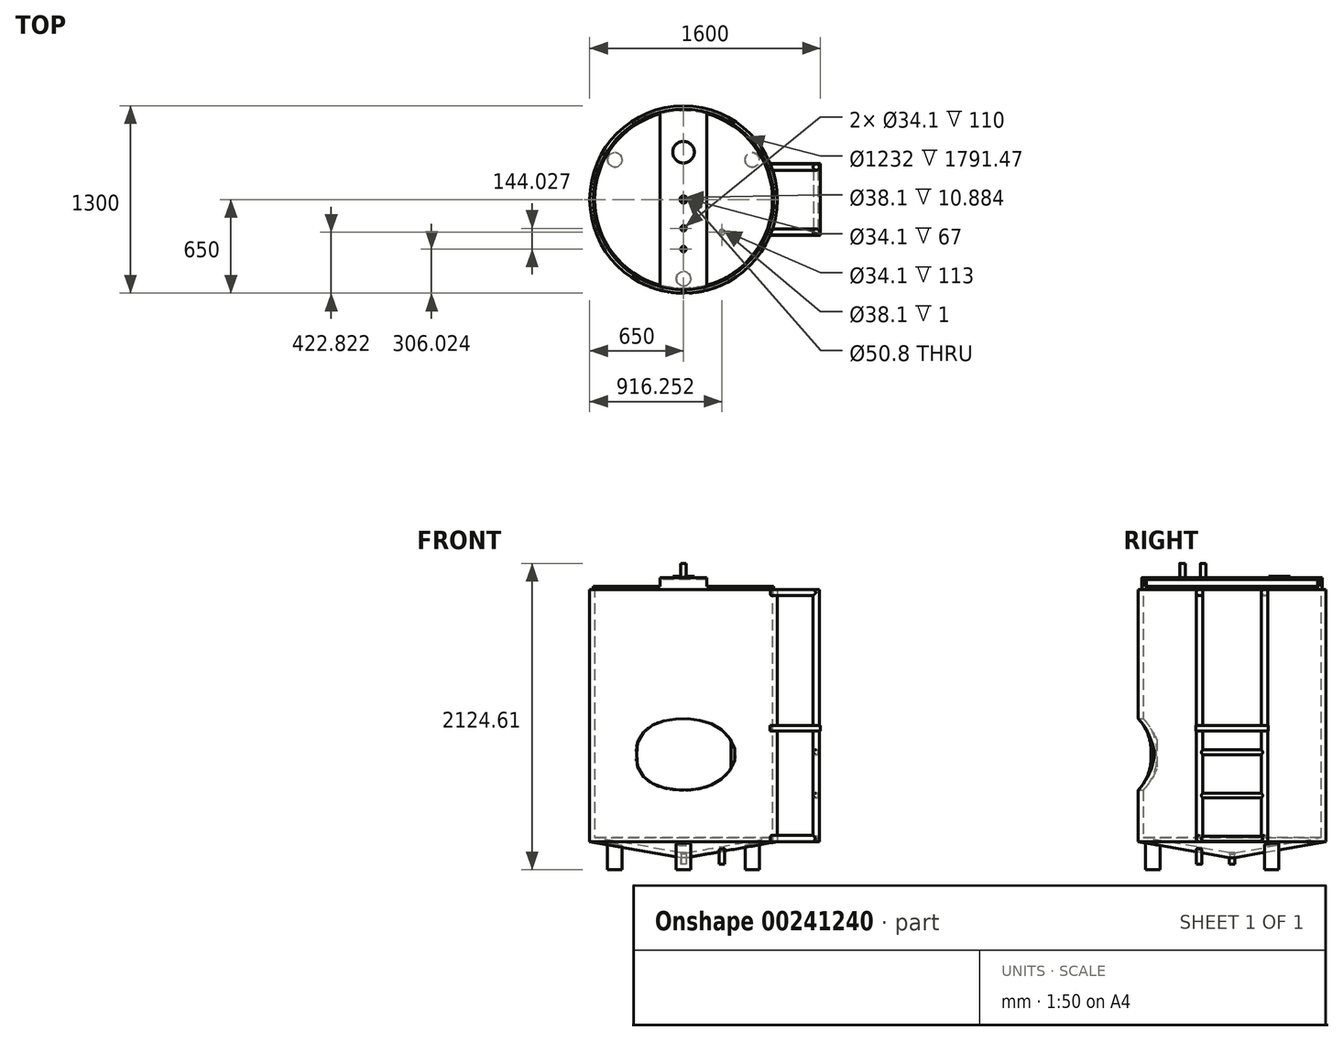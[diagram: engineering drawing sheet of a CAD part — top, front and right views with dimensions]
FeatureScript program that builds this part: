
annotation { "Feature Type Name" : "Feature", "Feature Type Description" : "" }
export const myFeature = defineFeature(function(context is Context, id is Id, definition is map)
    precondition{}
    {
        {
            var Q0;
            Q0=qCreatedBy(makeId("Front.planeOp"),FACE);
            var sketch = newSketch(context, id + "F0", { "sketchPlane" : qUnion([Q0])});
            skLineSegment(sketch, "E0", {"start": v(0, 0) * mm, "end": v(650, 114.61) * mm});
            skLineSegment(sketch, "E1", {"start": v(650, 114.61) * mm, "end": v(650, 1864.61) * mm});
            skLineSegment(sketch, "E2", {"start": v(650, 1864.61) * mm, "end": v(0, 1864.61) * mm});
            skLineSegment(sketch, "E3", {"start": v(0, 0) * mm, "end": v(0, 1864.61) * mm});
            skSolve(sketch);
        }
        {
            var Q0;
            Q0 = qSketchRegion(id + "F0", true);
            var Q1;
            Q1=sQuery(id+"F0.wireOp",EDGE,"E3");
            revolve(context, id + "F1", {"entities" : qUnion([Q0]), "axis" : qUnion([Q1]), "revolveType" : RevolveType.FULL});
        }
        {
            var Q0;
            Q0=makeQuery(id+"F1.opRevolve","SWEPT_FACE",FACE,{"disambiguationData":[OSD([sQuery(id+"F0.wireOp",EDGE,"E2")])]});
            shell(context, id + "F2", {"entities" : qUnion([Q0]), "thickness" : 34 * mm});
        }
        {
            var Q0;
            Q0=qCreatedBy(makeId("Top.planeOp"),FACE);
            cPlane(context, id + "F3", {"entities" : qUnion([Q0]), "cplaneType" : CPlaneType.OFFSET, "offset" : 280 * mm, "oppositeDirection" : true, "width" : 150 * mm, "height" : 150 * mm});
        }
        {
            var Q0;
            Q0=qCreatedBy(id+"F3.planeOp",FACE);
            var sketch = newSketch(context, id + "F4", { "sketchPlane" : qUnion([Q0])});
            skCircle(sketch, "E4", {"center": v(0, -550) * mm, "radius": 50 * mm});
            skCircle(sketch, "E5", {"center": v(476.31, 275) * mm, "radius": 50 * mm});
            skCircle(sketch, "E6", {"center": v(-476.31, 275) * mm, "radius": 50 * mm});
            skSolve(sketch);
        }
        {
            var Q0;
            Q0 = qSketchRegion(id + "F4", true);
            var Q1;
            Q1=makeQuery(id+"F1.opRevolve","SWEPT_BODY",BODY,{"disambiguationData":[OSD([sQuery(id+"F0.wireOp",EDGE,"E0"),sQuery(id+"F0.wireOp",EDGE,"E1"),sQuery(id+"F0.wireOp",EDGE,"E2"),sQuery(id+"F0.wireOp",EDGE,"E3")])]});
            extrude(context, id + "F5", {"entities" : qUnion([Q0]), "operationType" : NewBodyOperationType.ADD, "endBound" : BoundingType.UP_TO_BODY, "endBoundEntityBody" : qUnion([Q1]), "depth" : 25 * mm});
        }
        {
            var Q0;
            Q0=makeQuery(id+"F5.opExtrude","CAP_FACE",FACE,{"disambiguationData":[OSD([sQuery(id+"F4.wireOp",EDGE,"E5")])],"isStart":true});
            var sketch = newSketch(context, id + "F6", { "sketchPlane" : qUnion([Q0])});
            skCircle(sketch, "E7.0", {"center": v(476.31, -275) * mm, "radius": 50 * mm});
            skCircle(sketch, "E8.0", {"center": v(0, 550) * mm, "radius": 50 * mm});
            skCircle(sketch, "E9.0", {"center": v(-476.31, -275) * mm, "radius": 50 * mm});
            skSolve(sketch);
        }
        {
            var Q0;
            Q0 = qSketchRegion(id + "F6", true);
            extrude(context, id + "F7", {"entities" : qUnion([Q0]), "operationType" : NewBodyOperationType.REMOVE, "oppositeDirection" : true, "depth" : 200 * mm});
        }
        {
            var Q0;
            Q0=qCreatedBy(makeId("Top.planeOp"),FACE);
            var sketch = newSketch(context, id + "F8", { "sketchPlane" : qUnion([Q0])});
            skCircle(sketch, "E10", {"center": v(0, 0) * mm, "radius": 19.05 * mm});
            skCircle(sketch, "E11", {"center": v(266.25, -227.18) * mm, "radius": 19.05 * mm});
            skSolve(sketch);
        }
        {
            var Q0;
            Q0 = qSketchRegion(id + "F8", true);
            extrude(context, id + "F9", {"entities" : qUnion([Q0]), "operationType" : NewBodyOperationType.REMOVE, "depth" : 74 * mm});
        }
        {
            var Q0;
            Q0=makeQuery(id+"F1.opRevolve","SWEPT_FACE",FACE,{"disambiguationData":[OSD([sQuery(id+"F0.wireOp",EDGE,"E2")])]});
            var sketch = newSketch(context, id + "F10", { "sketchPlane" : qUnion([Q0])});
            skCircle(sketch, "E12.0", {"center": v(0, 0) * mm, "radius": 616 * mm});
            skCircle(sketch, "E13.0", {"center": v(0, 0) * mm, "radius": 626 * mm});
            skSolve(sketch);
        }
        {
            var Q0;
            Q0 = qSketchRegion(id + "F10", true);
            extrude(context, id + "F11", {"entities" : qUnion([Q0]), "operationType" : NewBodyOperationType.ADD, "depth" : 20 * mm});
        }
        {
            var Q0;
            Q0=qCreatedBy(makeId("Front.planeOp"),FACE);
            cPlane(context, id + "F12", {"entities" : qUnion([Q0]), "cplaneType" : CPlaneType.OFFSET, "offset" : 670 * mm, "width" : 150 * mm, "height" : 150 * mm});
        }
        {
            var Q0;
            Q0=qCreatedBy(id+"F12.planeOp",FACE);
            var sketch = newSketch(context, id + "F13", { "sketchPlane" : qUnion([Q0])});
            skLineSegment(sketch, "E14", {"start": v(0, 720) * mm, "end": v(325, 720) * mm});
            skLineSegment(sketch, "E15", {"start": v(0, 720) * mm, "end": v(-325, 720) * mm});
            skLineSegment(sketch, "E16", {"start": v(0, 720) * mm, "end": v(0, 945) * mm});
            skLineSegment(sketch, "E17", {"start": v(0, 720) * mm, "end": v(0, 495) * mm});
            skLineSegment(sketch, "E18", {"start": v(234.5, 720) * mm, "end": v(234.5, 875.8) * mm});
            skLineSegment(sketch, "E19", {"start": v(234.5, 720) * mm, "end": v(234.5, 564.2) * mm});
            skLineSegment(sketch, "E20", {"start": v(-234.5, 720) * mm, "end": v(-234.5, 875.8) * mm});
            skLineSegment(sketch, "E21", {"start": v(-234.5, 720) * mm, "end": v(-234.5, 564.2) * mm});
            skFitSpline(sketch, "E22", {"points": [v(-325, 720) * mm, v(-234.5, 875.8) * mm, v(0, 945) * mm, v(234.5, 875.8) * mm, v(325, 720) * mm, v(234.5, 564.2) * mm, v(0, 495) * mm, v(-234.5, 564.2) * mm, v(-325, 720) * mm]});
            skFitSpline(sketch, "E23.0", {"points": [v(-334.9, 713.7) * mm, v(-335.05, 720) * mm, v(-334.9, 726.3) * mm, v(-334.38, 734.68) * mm, v(-333.06, 745.1) * mm, v(-330.5, 757.5) * mm, v(-325.81, 773.84) * mm, v(-317.72, 793.8) * mm, v(-304.75, 816.76) * mm, v(-288.86, 838.5) * mm, v(-273.43, 855.42) * mm, v(-259.92, 868.1) * mm, v(-249.25, 877.16) * mm, v(-238.06, 885.74) * mm, v(-226.41, 893.8) * mm, v(-214.33, 901.33) * mm, v(-197.68, 910.7) * mm, v(-175.93, 921.14) * mm, v(-148.54, 931.68) * mm, v(-110.62, 943.1) * mm, v(-71, 950.64) * mm, v(-30.55, 954.38) * mm, v(0, 955.31) * mm, v(30.55, 954.38) * mm, v(71, 950.64) * mm, v(110.62, 943.1) * mm, v(148.54, 931.68) * mm, v(175.93, 921.14) * mm, v(197.68, 910.7) * mm, v(214.33, 901.33) * mm, v(226.41, 893.8) * mm, v(238.06, 885.74) * mm, v(249.25, 877.16) * mm, v(259.92, 868.1) * mm, v(273.43, 855.42) * mm, v(288.86, 838.5) * mm, v(304.75, 816.76) * mm, v(317.72, 793.8) * mm, v(325.81, 773.84) * mm, v(330.5, 757.5) * mm, v(333.06, 745.1) * mm, v(334.38, 734.68) * mm, v(334.9, 726.3) * mm, v(335.05, 720) * mm, v(334.9, 713.7) * mm, v(334.38, 705.32) * mm, v(333.06, 694.9) * mm, v(330.5, 682.5) * mm, v(325.81, 666.16) * mm, v(317.72, 646.2) * mm, v(304.75, 623.24) * mm, v(288.86, 601.5) * mm, v(273.43, 584.58) * mm, v(259.92, 571.9) * mm, v(249.25, 562.84) * mm, v(238.06, 554.26) * mm, v(226.41, 546.2) * mm, v(214.33, 538.67) * mm, v(197.68, 529.3) * mm, v(175.93, 518.86) * mm, v(148.54, 508.32) * mm, v(110.62, 496.9) * mm, v(71, 489.36) * mm, v(30.55, 485.62) * mm, v(0, 484.69) * mm, v(-30.55, 485.62) * mm, v(-71, 489.36) * mm, v(-110.62, 496.9) * mm, v(-148.54, 508.32) * mm, v(-175.93, 518.86) * mm, v(-197.68, 529.3) * mm, v(-214.33, 538.67) * mm, v(-226.41, 546.2) * mm, v(-238.06, 554.26) * mm, v(-249.25, 562.84) * mm, v(-259.92, 571.9) * mm, v(-273.43, 584.58) * mm, v(-288.86, 601.5) * mm, v(-304.75, 623.24) * mm, v(-317.72, 646.2) * mm, v(-325.81, 666.16) * mm, v(-330.5, 682.5) * mm, v(-333.06, 694.9) * mm, v(-334.38, 705.32) * mm, v(-334.9, 713.7) * mm, v(-335.05, 720) * mm, v(-334.9, 726.3) * mm, v(-334.9, 713.7) * mm]});
            skSolve(sketch);
        }
        {
            var Q0;
            Q0 = qSketchRegion(id + "F13", true);
            var Q1;
            Q1=makeQuery(id+"F1.opRevolve","SWEPT_BODY",BODY,{"disambiguationData":[OSD([sQuery(id+"F0.wireOp",EDGE,"E0"),sQuery(id+"F0.wireOp",EDGE,"E1"),sQuery(id+"F0.wireOp",EDGE,"E2"),sQuery(id+"F0.wireOp",EDGE,"E3")])]});
            extrude(context, id + "F14", {"entities" : qUnion([Q0]), "operationType" : NewBodyOperationType.ADD, "endBound" : BoundingType.UP_TO_BODY, "oppositeDirection" : true, "endBoundEntityBody" : qUnion([Q1]), "depth" : 25 * mm});
        }
        {
            var Q0;
            Q0=makeQuery(id+"F14.opExtrude","CAP_FACE",FACE,{"disambiguationData":[OSD([sQuery(id+"F13.wireOp",EDGE,"E22"),sQuery(id+"F13.wireOp",EDGE,"E23.0")])],"isStart":true});
            var sketch = newSketch(context, id + "F15", { "sketchPlane" : qUnion([Q0])});
            skFitSpline(sketch, "E24.0", {"points": [v(-325, 720) * mm, v(-325, 777.87) * mm, v(-245.57, 903.14) * mm, v(0, 967.52) * mm, v(245.57, 903.14) * mm, v(361.7, 720) * mm, v(245.57, 536.86) * mm, v(0, 472.48) * mm, v(-245.57, 536.86) * mm, v(-325, 662.13) * mm, v(-325, 720) * mm]});
            skSolve(sketch);
        }
        {
            var Q0;
            Q0 = qSketchRegion(id + "F15", true);
            extrude(context, id + "F16", {"entities" : qUnion([Q0]), "operationType" : NewBodyOperationType.REMOVE, "oppositeDirection" : true, "depth" : 149 * mm});
        }
        {
            var Q0;
            Q0=qCreatedBy(makeId("Right.planeOp"),FACE);
            cPlane(context, id + "F17", {"entities" : qUnion([Q0]), "cplaneType" : CPlaneType.OFFSET, "offset" : 950 * mm, "width" : 150 * mm, "height" : 150 * mm});
        }
        {
            var Q0;
            Q0=qCreatedBy(id+"F17.planeOp",FACE);
            var sketch = newSketch(context, id + "F18", { "sketchPlane" : qUnion([Q0])});
            skLineSegment(sketch, "E25.0", {"start": v(-626, 1884.61) * mm, "end": v(626, 1884.61) * mm});
            skLineSegment(sketch, "E26", {"start": v(0, 920) * mm, "end": v(250, 920) * mm});
            skLineSegment(sketch, "E27", {"start": v(0, 920) * mm, "end": v(-250, 920) * mm});
            skLineSegment(sketch, "E28", {"start": v(-250, 920) * mm, "end": v(-250, 882) * mm});
            skLineSegment(sketch, "E29", {"start": v(-250, 882) * mm, "end": v(250, 882) * mm});
            skLineSegment(sketch, "E30", {"start": v(250, 882) * mm, "end": v(250, 920) * mm});
            skSolve(sketch);
        }
        {
            var Q0;
            Q0 = qSketchRegion(id + "F18", true);
            var Q1;
            Q1=makeQuery(id+"F1.opRevolve","SWEPT_BODY",BODY,{"disambiguationData":[OSD([sQuery(id+"F0.wireOp",EDGE,"E0"),sQuery(id+"F0.wireOp",EDGE,"E1"),sQuery(id+"F0.wireOp",EDGE,"E2"),sQuery(id+"F0.wireOp",EDGE,"E3")])]});
            extrude(context, id + "F19", {"entities" : qUnion([Q0]), "operationType" : NewBodyOperationType.ADD, "endBound" : BoundingType.UP_TO_BODY, "oppositeDirection" : true, "endBoundEntityBody" : qUnion([Q1]), "depth" : 25 * mm});
        }
        {
            var Q0;
            Q0=makeQuery(id+"F19.opExtrude","SWEPT_FACE",FACE,{"disambiguationData":[OSD([sQuery(id+"F18.wireOp",EDGE,"E29")])]});
            var sketch = newSketch(context, id + "F20", { "sketchPlane" : qUnion([Q0])});
            skCircle(sketch, "E31", {"center": v(920, 225) * mm, "radius": 21.5 * mm});
            skCircle(sketch, "E32", {"center": v(920, -225) * mm, "radius": 21.5 * mm});
            skSolve(sketch);
        }
        {
            var Q0;
            Q0 = qSketchRegion(id + "F20", true);
            extrude(context, id + "F21", {"entities" : qUnion([Q0]), "operationType" : NewBodyOperationType.ADD, "depth" : 767 * mm, "hasSecondDirection" : true, "secondDirectionOppositeDirection" : true, "secondDirectionDepth" : 982.3 * mm});
        }
        {
            var Q0;
            Q0=qCreatedBy(id+"F17.planeOp",FACE);
            cPlane(context, id + "F22", {"entities" : qUnion([Q0]), "cplaneType" : CPlaneType.OFFSET, "offset" : 160 * mm, "oppositeDirection" : true, "width" : 150 * mm, "height" : 150 * mm});
        }
        {
            var Q0;
            Q0=qCreatedBy(id+"F22.planeOp",FACE);
            var sketch = newSketch(context, id + "F23", { "sketchPlane" : qUnion([Q0])});
            skLineSegment(sketch, "E33.0", {"start": v(246.5, 115) * mm, "end": v(203.5, 115) * mm});
            skLineSegment(sketch, "E34", {"start": v(-225, 115) * mm, "end": v(-225, 136.5) * mm});
            skCircle(sketch, "E35", {"center": v(-225, 136.5) * mm, "radius": 21.5 * mm});
            skLineSegment(sketch, "E36", {"start": v(225, 115) * mm, "end": v(225, 136.5) * mm});
            skCircle(sketch, "E37", {"center": v(225, 136.5) * mm, "radius": 21.5 * mm});
            skLineSegment(sketch, "E38", {"start": v(-225, 1864.3) * mm, "end": v(-225, 1842.8) * mm});
            skCircle(sketch, "E39", {"center": v(-225, 1842.8) * mm, "radius": 21.5 * mm});
            skLineSegment(sketch, "E40", {"start": v(225, 1864.3) * mm, "end": v(225, 1842.8) * mm});
            skCircle(sketch, "E41", {"center": v(225, 1842.8) * mm, "radius": 21.5 * mm});
            skSolve(sketch);
        }
        {
            var Q0;
            Q0 = qSketchRegion(id + "F23", true);
            var Q1;
            Q1=makeQuery(id+"F1.opRevolve","SWEPT_BODY",BODY,{"disambiguationData":[OSD([sQuery(id+"F0.wireOp",EDGE,"E0"),sQuery(id+"F0.wireOp",EDGE,"E1"),sQuery(id+"F0.wireOp",EDGE,"E2"),sQuery(id+"F0.wireOp",EDGE,"E3")])]});
            var Q2;
            Q2=makeQuery(id+"F1.opRevolve","SWEPT_BODY",BODY,{"disambiguationData":[OSD([sQuery(id+"F0.wireOp",EDGE,"E0"),sQuery(id+"F0.wireOp",EDGE,"E1"),sQuery(id+"F0.wireOp",EDGE,"E2"),sQuery(id+"F0.wireOp",EDGE,"E3")])]});
            extrude(context, id + "F24", {"entities" : qUnion([Q0]), "operationType" : NewBodyOperationType.ADD, "endBound" : BoundingType.UP_TO_BODY, "endBoundEntityBody" : qUnion([Q1]), "depth" : 25 * mm, "hasSecondDirection" : true, "secondDirectionBound" : SecondDirectionBoundingType.UP_TO_BODY, "secondDirectionOppositeDirection" : true, "secondDirectionBoundEntityBody" : qUnion([Q2]), "secondDirectionDepth" : 25 * mm});
        }
        {
            var Q0;
            Q0=qCreatedBy(makeId("Front.planeOp"),FACE);
            var sketch = newSketch(context, id + "F25", { "sketchPlane" : qUnion([Q0])});
            skLineSegment(sketch, "E42.0", {"start": v(941.5, 115) * mm, "end": v(898.5, 115) * mm});
            skLineSegment(sketch, "E43.0", {"start": v(941.5, 1864.3) * mm, "end": v(898.5, 1864.3) * mm});
            skLineSegment(sketch, "E44", {"start": v(920, 1864.3) * mm, "end": v(920, 115) * mm});
            skCircle(sketch, "E45", {"center": v(920, 135) * mm, "radius": 17 * mm});
            skCircle(sketch, "E46", {"center": v(920, 435) * mm, "radius": 17 * mm});
            skCircle(sketch, "E47", {"center": v(920, 735) * mm, "radius": 17 * mm});
            skSolve(sketch);
        }
        {
            var Q0;
            Q0 = qSketchRegion(id + "F25", true);
            var Q1;
            Q1=makeQuery(id+"F1.opRevolve","SWEPT_BODY",BODY,{"disambiguationData":[OSD([sQuery(id+"F0.wireOp",EDGE,"E0"),sQuery(id+"F0.wireOp",EDGE,"E1"),sQuery(id+"F0.wireOp",EDGE,"E2"),sQuery(id+"F0.wireOp",EDGE,"E3")])]});
            var Q2;
            Q2=makeQuery(id+"F1.opRevolve","SWEPT_BODY",BODY,{"disambiguationData":[OSD([sQuery(id+"F0.wireOp",EDGE,"E0"),sQuery(id+"F0.wireOp",EDGE,"E1"),sQuery(id+"F0.wireOp",EDGE,"E2"),sQuery(id+"F0.wireOp",EDGE,"E3")])]});
            extrude(context, id + "F26", {"entities" : qUnion([Q0]), "operationType" : NewBodyOperationType.ADD, "endBound" : BoundingType.UP_TO_BODY, "endBoundEntityBody" : qUnion([Q1]), "depth" : 25 * mm, "hasSecondDirection" : true, "secondDirectionBound" : SecondDirectionBoundingType.UP_TO_BODY, "secondDirectionOppositeDirection" : true, "secondDirectionBoundEntityBody" : qUnion([Q2]), "secondDirectionDepth" : 25 * mm});
        }
        {
            var Q0;
            Q0=qCreatedBy(id+"F3.planeOp",FACE);
            cPlane(context, id + "F27", {"entities" : qUnion([Q0]), "cplaneType" : CPlaneType.OFFSET, "offset" : 240 * mm, "width" : 150 * mm, "height" : 150 * mm});
        }
        {
            var Q0;
            Q0=qCreatedBy(id+"F27.planeOp",FACE);
            var sketch = newSketch(context, id + "F28", { "sketchPlane" : qUnion([Q0])});
            skCircle(sketch, "E48.0", {"center": v(0, 0) * mm, "radius": 19.05 * mm});
            skCircle(sketch, "E49.0", {"center": v(0, 0) * mm, "radius": 17.05 * mm});
            skSolve(sketch);
        }
        {
            var Q0;
            Q0 = qSketchRegion(id + "F28", true);
            extrude(context, id + "F29", {"entities" : qUnion([Q0]), "operationType" : NewBodyOperationType.ADD, "depth" : 67 * mm});
        }
        {
            var Q0;
            Q0=qCreatedBy(id+"F27.planeOp",FACE);
            var sketch = newSketch(context, id + "F30", { "sketchPlane" : qUnion([Q0])});
            skCircle(sketch, "E50.0", {"center": v(266.25, -227.18) * mm, "radius": 19.05 * mm});
            skCircle(sketch, "E51.0", {"center": v(266.25, -227.18) * mm, "radius": 17.05 * mm});
            skSolve(sketch);
        }
        {
            var Q0;
            Q0 = qSketchRegion(id + "F30", true);
            extrude(context, id + "F31", {"entities" : qUnion([Q0]), "operationType" : NewBodyOperationType.ADD, "depth" : 113 * mm});
        }
        {
            var Q0;
            Q0=makeQuery(id+"F11.opExtrude","CAP_FACE",FACE,{"disambiguationData":[OSD([sQuery(id+"F10.wireOp",EDGE,"E12.0"),sQuery(id+"F10.wireOp",EDGE,"E13.0")])],"isStart":false});
            var sketch = newSketch(context, id + "F32", { "sketchPlane" : qUnion([Q0])});
            skArc(sketch, "E52.0", {"start": v(-162.02, -594.31) * mm, "mid": v(0, -616) * mm, "end": v(162.02, -594.31) * mm});
            skArc(sketch, "E53.0", {"start": v(-162.02, -604.67) * mm, "mid": v(0, -626) * mm, "end": v(162.02, -604.67) * mm});
            skArc(sketch, "E54.trimOffspring", {"start": v(162.02, 604.67) * mm, "mid": v(0, 626) * mm, "end": v(-162.02, 604.67) * mm});
            skLineSegment(sketch, "E55", {"start": v(-162.02, 604.67) * mm, "end": v(-162.02, 594.31) * mm});
            skLineSegment(sketch, "E56", {"start": v(162.02, 604.67) * mm, "end": v(162.02, 594.31) * mm});
            skArc(sketch, "E57.0", {"start": v(162.02, 594.31) * mm, "mid": v(0, 616) * mm, "end": v(-162.02, 594.31) * mm});
            skLineSegment(sketch, "E58.trimOffspring", {"start": v(-162.02, -594.31) * mm, "end": v(-162.02, -604.67) * mm});
            skLineSegment(sketch, "E59.trimOffspring", {"start": v(162.02, -594.31) * mm, "end": v(162.02, -604.67) * mm});
            skSolve(sketch);
        }
        {
            var Q0;
            Q0 = qSketchRegion(id + "F32", true);
            extrude(context, id + "F33", {"entities" : qUnion([Q0]), "operationType" : NewBodyOperationType.ADD, "depth" : 60 * mm});
        }
        {
            var Q0;
            Q0=makeQuery(id+"F33.opExtrude","CAP_FACE",FACE,{"disambiguationData":[OSD([sQuery(id+"F32.wireOp",EDGE,"E52.0"),sQuery(id+"F32.wireOp",EDGE,"E53.0"),sQuery(id+"F32.wireOp",EDGE,"9d0d0737-57ff-40db-b769-893f6e7693da.trimOffspring"),sQuery(id+"F32.wireOp",EDGE,"cf01eeaf-4652-4ba8-9705-34391afd7a9d.trimOffspring")])],"isStart":false});
            var sketch = newSketch(context, id + "F34", { "sketchPlane" : qUnion([Q0])});
            skLineSegment(sketch, "E60.0", {"start": v(-162.02, -604.67) * mm, "end": v(-162.02, -604.67) * mm});
            skLineSegment(sketch, "E61.0", {"start": v(162.02, 604.67) * mm, "end": v(162.02, 604.67) * mm});
            skArc(sketch, "E62.0", {"start": v(-162.02, -604.67) * mm, "mid": v(0, -626) * mm, "end": v(162.02, -604.67) * mm});
            skArc(sketch, "E63.0", {"start": v(162.02, 604.67) * mm, "mid": v(0, 626) * mm, "end": v(-162.02, 604.67) * mm});
            skLineSegment(sketch, "E64", {"start": v(-162.02, 604.67) * mm, "end": v(-162.02, -604.67) * mm});
            skLineSegment(sketch, "E65", {"start": v(162.02, 604.67) * mm, "end": v(162.02, -604.67) * mm});
            skSolve(sketch);
        }
        {
            var Q0;
            Q0 = qSketchRegion(id + "F34", true);
            extrude(context, id + "F35", {"entities" : qUnion([Q0]), "operationType" : NewBodyOperationType.ADD, "oppositeDirection" : true, "depth" : 10 * mm});
        }
        {
            var Q0;
            Q0=makeQuery(id+"F35.boolean.opBoolean","MERGE",FACE,{"derivedFrom":[makeQuery(id+"F33.opExtrude","CAP_FACE",FACE,{"disambiguationData":[OSD([sQuery(id+"F32.wireOp",EDGE,"E52.0"),sQuery(id+"F32.wireOp",EDGE,"E53.0"),sQuery(id+"F32.wireOp",EDGE,"E58.trimOffspring"),sQuery(id+"F32.wireOp",EDGE,"E59.trimOffspring")])],"isStart":false}),makeQuery(id+"F33.opExtrude","CAP_FACE",FACE,{"disambiguationData":[OSD([sQuery(id+"F32.wireOp",EDGE,"E54.trimOffspring"),sQuery(id+"F32.wireOp",EDGE,"E55"),sQuery(id+"F32.wireOp",EDGE,"E56"),sQuery(id+"F32.wireOp",EDGE,"E57.0")])],"isStart":false}),makeQuery(id+"F35.opExtrude","CAP_FACE",FACE,{"disambiguationData":[OSD([sQuery(id+"F34.wireOp",EDGE,"E62.0"),sQuery(id+"F34.wireOp",EDGE,"E63.0"),sQuery(id+"F34.wireOp",EDGE,"E64"),sQuery(id+"F34.wireOp",EDGE,"E65")])],"isStart":true})]});
            var sketch = newSketch(context, id + "F36", { "sketchPlane" : qUnion([Q0])});
            skCircle(sketch, "E66", {"center": v(0, 0) * mm, "radius": 25.4 * mm});
            skCircle(sketch, "E67", {"center": v(0, -199.95) * mm, "radius": 19.05 * mm});
            skCircle(sketch, "E68", {"center": v(0, -343.98) * mm, "radius": 19.05 * mm});
            skCircle(sketch, "E69", {"center": v(0, 378.25) * mm, "radius": 75 * mm});
            skSolve(sketch);
        }
        {
            var Q0;
            Q0=makeQuery(id+"F36.imprint","IMPRINT",FACE,{"disambiguationData":[TD([[makeQuery(id+"F36.imprint","IMPRINT",EDGE,{"derivedFrom":sQuery(id+"F36.wireOp",EDGE,"E68")}),1.0]])]});
            var Q1;
            Q1=makeQuery(id+"F36.imprint","IMPRINT",FACE,{"disambiguationData":[TD([[makeQuery(id+"F36.imprint","IMPRINT",EDGE,{"derivedFrom":sQuery(id+"F36.wireOp",EDGE,"E67")}),1.0]])]});
            var Q2;
            Q2=makeQuery(id+"F36.imprint","IMPRINT",FACE,{"disambiguationData":[TD([[makeQuery(id+"F36.imprint","IMPRINT",EDGE,{"derivedFrom":sQuery(id+"F36.wireOp",EDGE,"E66")}),1.0]])]});
            var Q3;
            Q3=sQuery(id+"F36.wireOp",EDGE,"E66");
            var Q4;
            Q4=sQuery(id+"F36.wireOp",EDGE,"E67");
            var Q5;
            Q5=sQuery(id+"F36.wireOp",EDGE,"E68");
            extrude(context, id + "F37", {"entities" : qUnion([Q0, Q1, Q2]), "operationType" : NewBodyOperationType.REMOVE, "surfaceEntities" : qUnion([Q3, Q4, Q5]), "oppositeDirection" : true, "depth" : 47 * mm});
        }
        {
            var Q0;
            Q0=makeQuery(id+"F35.boolean.opBoolean","MERGE",FACE,{"derivedFrom":[makeQuery(id+"F33.opExtrude","CAP_FACE",FACE,{"disambiguationData":[OSD([sQuery(id+"F32.wireOp",EDGE,"E52.0"),sQuery(id+"F32.wireOp",EDGE,"E53.0"),sQuery(id+"F32.wireOp",EDGE,"E58.trimOffspring"),sQuery(id+"F32.wireOp",EDGE,"E59.trimOffspring")])],"isStart":false}),makeQuery(id+"F33.opExtrude","CAP_FACE",FACE,{"disambiguationData":[OSD([sQuery(id+"F32.wireOp",EDGE,"E54.trimOffspring"),sQuery(id+"F32.wireOp",EDGE,"E55"),sQuery(id+"F32.wireOp",EDGE,"E56"),sQuery(id+"F32.wireOp",EDGE,"E57.0")])],"isStart":false}),makeQuery(id+"F35.opExtrude","CAP_FACE",FACE,{"disambiguationData":[OSD([sQuery(id+"F34.wireOp",EDGE,"E62.0"),sQuery(id+"F34.wireOp",EDGE,"E63.0"),sQuery(id+"F34.wireOp",EDGE,"E64"),sQuery(id+"F34.wireOp",EDGE,"E65")])],"isStart":true})]});
            var sketch = newSketch(context, id + "F38", { "sketchPlane" : qUnion([Q0])});
            skCircle(sketch, "E70", {"center": v(0, 328.5) * mm, "radius": 75 * mm});
            skSolve(sketch);
        }
        {
            var Q0;
            Q0 = qSketchRegion(id + "F38", true);
            extrude(context, id + "F39", {"entities" : qUnion([Q0]), "operationType" : NewBodyOperationType.ADD, "depth" : 10 * mm});
        }
        {
            var Q0;
            Q0=makeQuery(id+"F35.boolean.opBoolean","MERGE",FACE,{"derivedFrom":[makeQuery(id+"F33.opExtrude","CAP_FACE",FACE,{"disambiguationData":[OSD([sQuery(id+"F32.wireOp",EDGE,"E52.0"),sQuery(id+"F32.wireOp",EDGE,"E53.0"),sQuery(id+"F32.wireOp",EDGE,"E58.trimOffspring"),sQuery(id+"F32.wireOp",EDGE,"E59.trimOffspring")])],"isStart":false}),makeQuery(id+"F33.opExtrude","CAP_FACE",FACE,{"disambiguationData":[OSD([sQuery(id+"F32.wireOp",EDGE,"E54.trimOffspring"),sQuery(id+"F32.wireOp",EDGE,"E55"),sQuery(id+"F32.wireOp",EDGE,"E56"),sQuery(id+"F32.wireOp",EDGE,"E57.0")])],"isStart":false}),makeQuery(id+"F35.opExtrude","CAP_FACE",FACE,{"disambiguationData":[OSD([sQuery(id+"F34.wireOp",EDGE,"E62.0"),sQuery(id+"F34.wireOp",EDGE,"E63.0"),sQuery(id+"F34.wireOp",EDGE,"E64"),sQuery(id+"F34.wireOp",EDGE,"E65")])],"isStart":true})]});
            var sketch = newSketch(context, id + "F40", { "sketchPlane" : qUnion([Q0])});
            skCircle(sketch, "E71.0", {"center": v(0, -199.95) * mm, "radius": 19.05 * mm});
            skCircle(sketch, "E72.0", {"center": v(0, -343.98) * mm, "radius": 19.05 * mm});
            skCircle(sketch, "E73.0", {"center": v(0, -199.95) * mm, "radius": 17.05 * mm});
            skCircle(sketch, "E74.0", {"center": v(0, -343.98) * mm, "radius": 17.05 * mm});
            skSolve(sketch);
        }
        {
            var Q0;
            Q0 = qSketchRegion(id + "F40", true);
            var Q1;
            Q1=makeQuery(id+"F35.opExtrude","CAP_FACE",FACE,{"disambiguationData":[OSD([sQuery(id+"F34.wireOp",EDGE,"E62.0"),sQuery(id+"F34.wireOp",EDGE,"E63.0"),sQuery(id+"F34.wireOp",EDGE,"E64"),sQuery(id+"F34.wireOp",EDGE,"E65")])],"isStart":false});
            extrude(context, id + "F41", {"entities" : qUnion([Q0]), "operationType" : NewBodyOperationType.ADD, "depth" : 100 * mm, "hasSecondDirection" : true, "secondDirectionBound" : SecondDirectionBoundingType.UP_TO_SURFACE, "secondDirectionOppositeDirection" : true, "secondDirectionBoundEntityFace" : qUnion([Q1]), "secondDirectionDepth" : 25 * mm});
        }
    });
